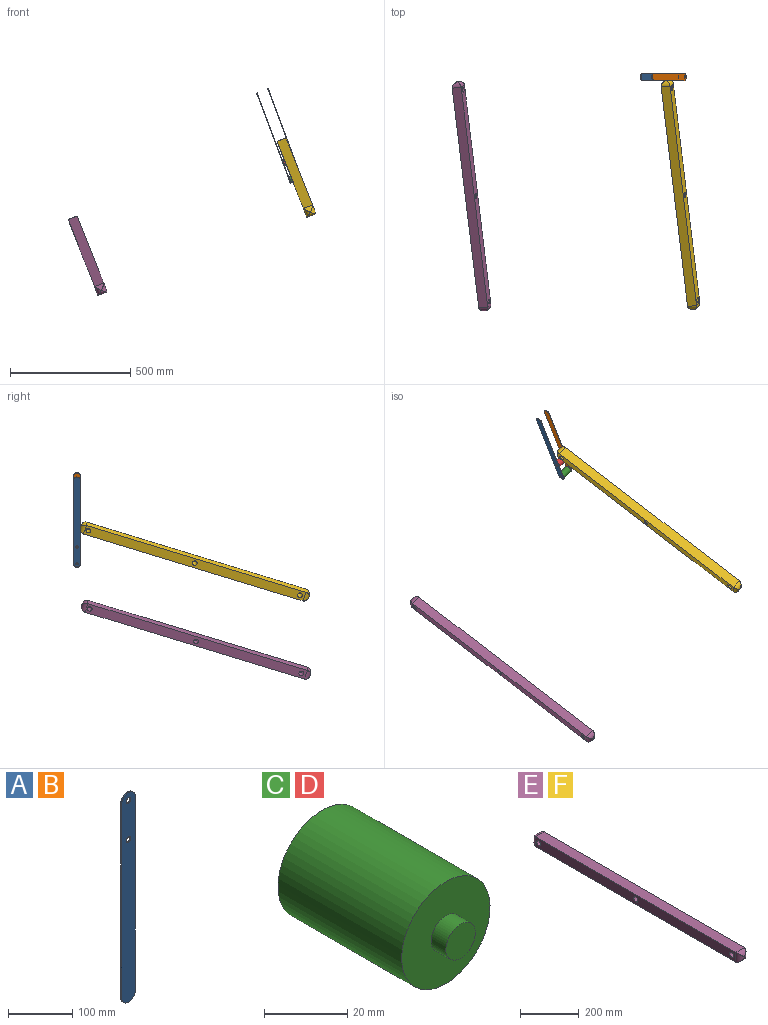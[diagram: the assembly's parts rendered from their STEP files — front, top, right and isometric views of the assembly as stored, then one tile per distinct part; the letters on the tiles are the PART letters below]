
ASSEMBLY  parts=6 mates=7
PART A: 8 faces, bbox 30x2x400 mm
  f0: cylinder r=15mm len=30mm, axis (0,1,0), area 94.2mm2, adj f1,f3,f4,f5
  f1: plane 370x2mm, normal (-1,0,0), area 740mm2, adj f0,f2,f4,f5
  f2: cylinder r=15mm len=30mm, axis (0,1,0), area 94.2mm2, adj f1,f3,f4,f5
  f3: plane 370x2mm, normal (1,0,0), area 740mm2, adj f0,f2,f4,f5
  f4: plane 400x30mm, normal (0,-1,0), area 11649.8mm2, adj f0,f1,f2,f3,f6,f7
  f5: plane 400x30mm, normal (0,1,0), area 11649.8mm2, adj f0,f1,f2,f3,f6,f7
  f6: cylinder r=5mm len=10mm, axis (0,-1,0), area 62.8mm2, adj f4,f5
  f7: cylinder r=5mm len=10mm, axis (0,-1,0), area 62.8mm2, adj f4,f5
PART B: same geometry as A
PART C: 7 faces, bbox 30x52x30 mm
  f0: cylinder r=15mm len=42mm, axis (0,1,0), area 3958.4mm2, adj f1,f2
  f1: plane 30x30mm, normal (0,-1,0), area 628.3mm2, adj f0,f5
  f2: plane 30x30mm, normal (0,1,0), area 628.3mm2, adj f0,f3
  f3: cylinder r=5mm len=10mm, axis (0,-1,0), area 157.1mm2, adj f2,f4
  f4: plane 10x10mm, normal (0,1,0), area 78.5mm2, adj f3
  f5: cylinder r=5mm len=10mm, axis (0,1,0), area 157.1mm2, adj f1,f6
  f6: plane 10x10mm, normal (0,-1,0), area 78.5mm2, adj f5
PART D: same geometry as C
PART E: 15 faces, bbox 40x1000x40 mm
  f0: plane 960x40mm, normal (-1,0,0), area 37457.5mm2, adj f1,f3,f4,f8,f12,f13,f14
  f1: plane 960x40mm, normal (0,0,-1), area 38400mm2, adj f0,f2,f5,f9
  f2: plane 960x40mm, normal (1,0,0), area 37457.5mm2, adj f1,f3,f7,f11,f12,f13,f14
  f3: plane 960x40mm, normal (0,0,1), area 38400mm2, adj f0,f2,f6,f10
  f4: cylinder r=20mm len=40mm, axis (0,0,1), area 800mm2, adj f0,f5,f6
  f5: cylinder r=20mm len=40mm, axis (-1,0,0), area 800mm2, adj f1,f4,f7
  f6: cylinder r=20mm len=40mm, axis (1,0,0), area 800mm2, adj f3,f4,f7
  f7: cylinder r=20mm len=40mm, axis (0,0,-1), area 800mm2, adj f2,f5,f6
  f8: cylinder r=20mm len=40mm, axis (0,0,-1), area 800mm2, adj f0,f9,f10
  f9: cylinder r=20mm len=40mm, axis (1,0,0), area 800mm2, adj f1,f8,f11
  f10: cylinder r=20mm len=40mm, axis (-1,0,0), area 800mm2, adj f3,f8,f11
  f11: cylinder r=20mm len=40mm, axis (0,0,1), area 800mm2, adj f2,f9,f10
  f12: cylinder r=10mm len=40mm, axis (-1,0,0), area 2513.3mm2, adj f0,f2
  f13: cylinder r=10mm len=40mm, axis (1,0,0), area 2513.3mm2, adj f0,f2
  f14: cylinder r=10mm len=40mm, axis (1,0,0), area 2513.3mm2, adj f0,f2
PART F: same geometry as E
PLACE A rot(axis=(-0.7,0.7,-0.13),165.6deg) t=(-339.65,280.29,197.53)mm
PLACE B rot(axis=(-0.7,0.7,-0.13),165.6deg) t=(-292.82,280.6,215.07)mm
PLACE C rot(axis=(-0.7,0.7,-0.13),165.6deg) t=(-200.04,295.32,-161.3)mm
PLACE D rot(axis=(-0.7,0.7,-0.13),165.6deg) t=(-226.28,295.32,-91.22)mm
PLACE E rot(axis=(0.66,-0.74,0.13),27.3deg) t=(-1112.04,281.19,-358.3)mm
PLACE F rot(axis=(0.66,-0.74,0.13),27.3deg) t=(-243.8,287,-33.16)mm
MATE parallel F.f13 <-> A.f0  axis (-0.94,-0.01,-0.35) through (-246.47,247.99,-25.34)mm
MATE revolute D.f3 <-> A.f7  axis (-0.94,-0.01,-0.35) through (-230.96,295.28,-92.98)mm
MATE revolute C.f3 <-> B.f0  axis (0.94,0.01,0.35) through (-156.02,295.61,-144.81)mm
MATE cylindrical F.f12 <-> E.f12  axis (0.94,0.01,0.35) through (-102.8,-631.3,-279.25)mm
MATE revolute C.f3 <-> A.f0  axis (-0.94,-0.01,-0.35) through (-204.72,295.28,-163.05)mm
MATE cylindrical F.f14 <-> E.f14  axis (0.94,0.01,0.35) through (-155.6,-194.12,-146.07)mm
MATE revolute D.f3 <-> B.f7  axis (0.94,0.01,0.35) through (-182.26,295.61,-74.74)mm
